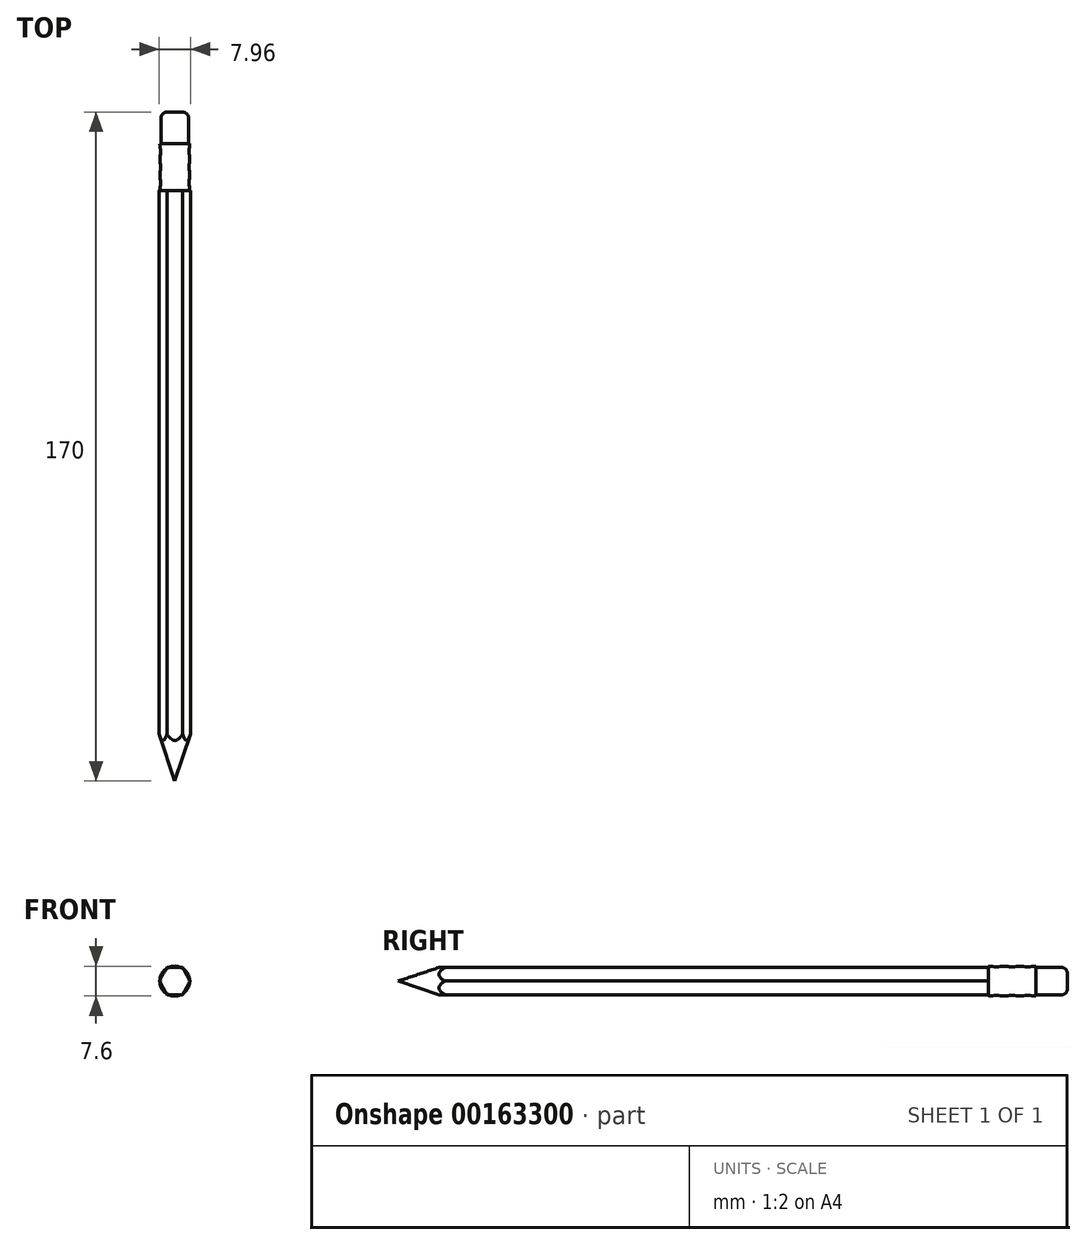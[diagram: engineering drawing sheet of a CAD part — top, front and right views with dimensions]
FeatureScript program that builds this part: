
annotation { "Feature Type Name" : "Feature", "Feature Type Description" : "" }
export const myFeature = defineFeature(function(context is Context, id is Id, definition is map)
    precondition{}
    {
        {
            var Q0;
            Q0=qCreatedBy(makeId("Front.planeOp"),FACE);
            var sketch = newSketch(context, id + "F0", { "sketchPlane" : qUnion([Q0])});
            skCircle(sketch, "E0.cCircle", {"center": v(0, 0) * mm, "radius": 3.45 * mm, "construction": true});
            skLineSegment(sketch, "E0.0", {"start": v(2, 3.45) * mm, "end": v(3.98, 0) * mm});
            skLineSegment(sketch, "E0.1", {"start": v(3.98, 0) * mm, "end": v(2, -3.45) * mm});
            skLineSegment(sketch, "E0.2", {"start": v(2, -3.45) * mm, "end": v(-2, -3.45) * mm});
            skLineSegment(sketch, "E0.3", {"start": v(-2, -3.45) * mm, "end": v(-3.98, 0) * mm});
            skLineSegment(sketch, "E0.4", {"start": v(-3.98, 0) * mm, "end": v(-2, 3.45) * mm});
            skLineSegment(sketch, "E0.5", {"start": v(-2, 3.45) * mm, "end": v(2, 3.45) * mm});
            skPoint(sketch, "E0.0.midPoint", {"position": v(2.99, 1.73) * mm});
            skSolve(sketch);
        }
        {
            var Q0;
            Q0 = qSketchRegion(id + "F0", true);
            extrude(context, id + "F1", {"entities" : qUnion([Q0]), "endBound" : BoundingType.SYMMETRIC, "depth" : 150 * mm});
        }
        {
            var Q0;
            Q0=qCreatedBy(makeId("Right.planeOp"),FACE);
            var sketch = newSketch(context, id + "F2", { "sketchPlane" : qUnion([Q0])});
            skLineSegment(sketch, "E1", {"start": v(-75, 0) * mm, "end": v(-60, 5) * mm});
            skLineSegment(sketch, "E2", {"start": v(-60, 5) * mm, "end": v(-75, 5) * mm});
            skLineSegment(sketch, "E3", {"start": v(-75, 5) * mm, "end": v(-75, 0) * mm});
            skLineSegment(sketch, "E4", {"start": v(-75, 0) * mm, "end": v(-60, 0) * mm, "construction": true});
            skSolve(sketch);
        }
        {
            var Q0;
            Q0 = qSketchRegion(id + "F2", true);
            var Q1;
            Q1=sQuery(id+"F2.wireOp",EDGE,"E4");
            revolve(context, id + "F3", {"entities" : qUnion([Q0]), "axis" : qUnion([Q1]), "revolveType" : RevolveType.ONE_DIRECTION, "oppositeDirection" : true, "angle" : 180 * degree});
        }
        {
            var Q0;
            Q0=makeQuery(id+"F3.opRevolve","SWEPT_BODY",BODY,{"disambiguationData":[OSD([sQuery(id+"F2.wireOp",EDGE,"E1"),sQuery(id+"F2.wireOp",EDGE,"E2"),sQuery(id+"F2.wireOp",EDGE,"E3")])]});
            var Q1;
            Q1=qCreatedBy(makeId("Right.planeOp"),FACE);
            mirror(context, id + "F4", {"entities" : qUnion([Q0]), "mirrorPlane" : qUnion([Q1])});
        }
        {
            var Q0;
            Q0=makeQuery(id+"F4.opPattern","COPY",BODY,{"derivedFrom":makeQuery(id+"F3.opRevolve","SWEPT_BODY",BODY,{"disambiguationData":[OSD([sQuery(id+"F2.wireOp",EDGE,"E1"),sQuery(id+"F2.wireOp",EDGE,"E2"),sQuery(id+"F2.wireOp",EDGE,"E3")])]}),"instanceName":"1"});
            var Q1;
            Q1=makeQuery(id+"F3.opRevolve","SWEPT_BODY",BODY,{"disambiguationData":[OSD([sQuery(id+"F2.wireOp",EDGE,"E1"),sQuery(id+"F2.wireOp",EDGE,"E2"),sQuery(id+"F2.wireOp",EDGE,"E3")])]});
            var Q2;
            Q2=makeQuery(id+"F1.opExtrude","SWEPT_BODY",BODY,{"disambiguationData":[OSD([sQuery(id+"F0.wireOp",EDGE,"E0.0"),sQuery(id+"F0.wireOp",EDGE,"E0.1"),sQuery(id+"F0.wireOp",EDGE,"E0.2"),sQuery(id+"F0.wireOp",EDGE,"E0.3"),sQuery(id+"F0.wireOp",EDGE,"E0.4"),sQuery(id+"F0.wireOp",EDGE,"E0.5")])]});
            booleanBodies(context, id + "F5", {"operationType" : BooleanOperationType.SUBTRACTION, "tools" : qUnion([Q0, Q1]), "targets" : qUnion([Q2])});
        }
        {
            var Q0;
            Q0=qCreatedBy(makeId("Right.planeOp"),FACE);
            var sketch = newSketch(context, id + "F6", { "sketchPlane" : qUnion([Q0])});
            skLineSegment(sketch, "E5", {"start": v(75, 3.8) * mm, "end": v(75, 0) * mm});
            skLineSegment(sketch, "E6", {"start": v(75, 0) * mm, "end": v(95, 0) * mm});
            skLineSegment(sketch, "E7", {"start": v(95, 0) * mm, "end": v(95, 2) * mm});
            skLineSegment(sketch, "E8", {"start": v(93.5, 3.5) * mm, "end": v(87, 3.5) * mm});
            skLineSegment(sketch, "E9", {"start": v(87, 3.5) * mm, "end": v(87, 3.8) * mm});
            skFitSpline(sketch, "E10", {"points": [v(87, 3.8) * mm, v(85, 3.6) * mm, v(83, 3.8) * mm, v(81, 3.6) * mm, v(79, 3.8) * mm, v(77, 3.6) * mm, v(75, 3.8) * mm], "startDerivative": vector(-18, 0) * mm, "endDerivative": vector(-18, 0) * mm});
            skPoint(sketch, "E11.visualSharp", {"position": v(95, 3.5) * mm});
            skArc(sketch, "E11.filletArc", {"start": v(95, 2) * mm, "mid": v(94.56, 3.06) * mm, "end": v(93.5, 3.5) * mm});
            skSolve(sketch);
        }
        {
            var Q0;
            Q0 = qSketchRegion(id + "F6", true);
            var Q1;
            Q1=sQuery(id+"F6.wireOp",EDGE,"E6");
            revolve(context, id + "F7", {"operationType" : NewBodyOperationType.ADD, "entities" : qUnion([Q0]), "axis" : qUnion([Q1]), "revolveType" : RevolveType.FULL});
        }
    });
